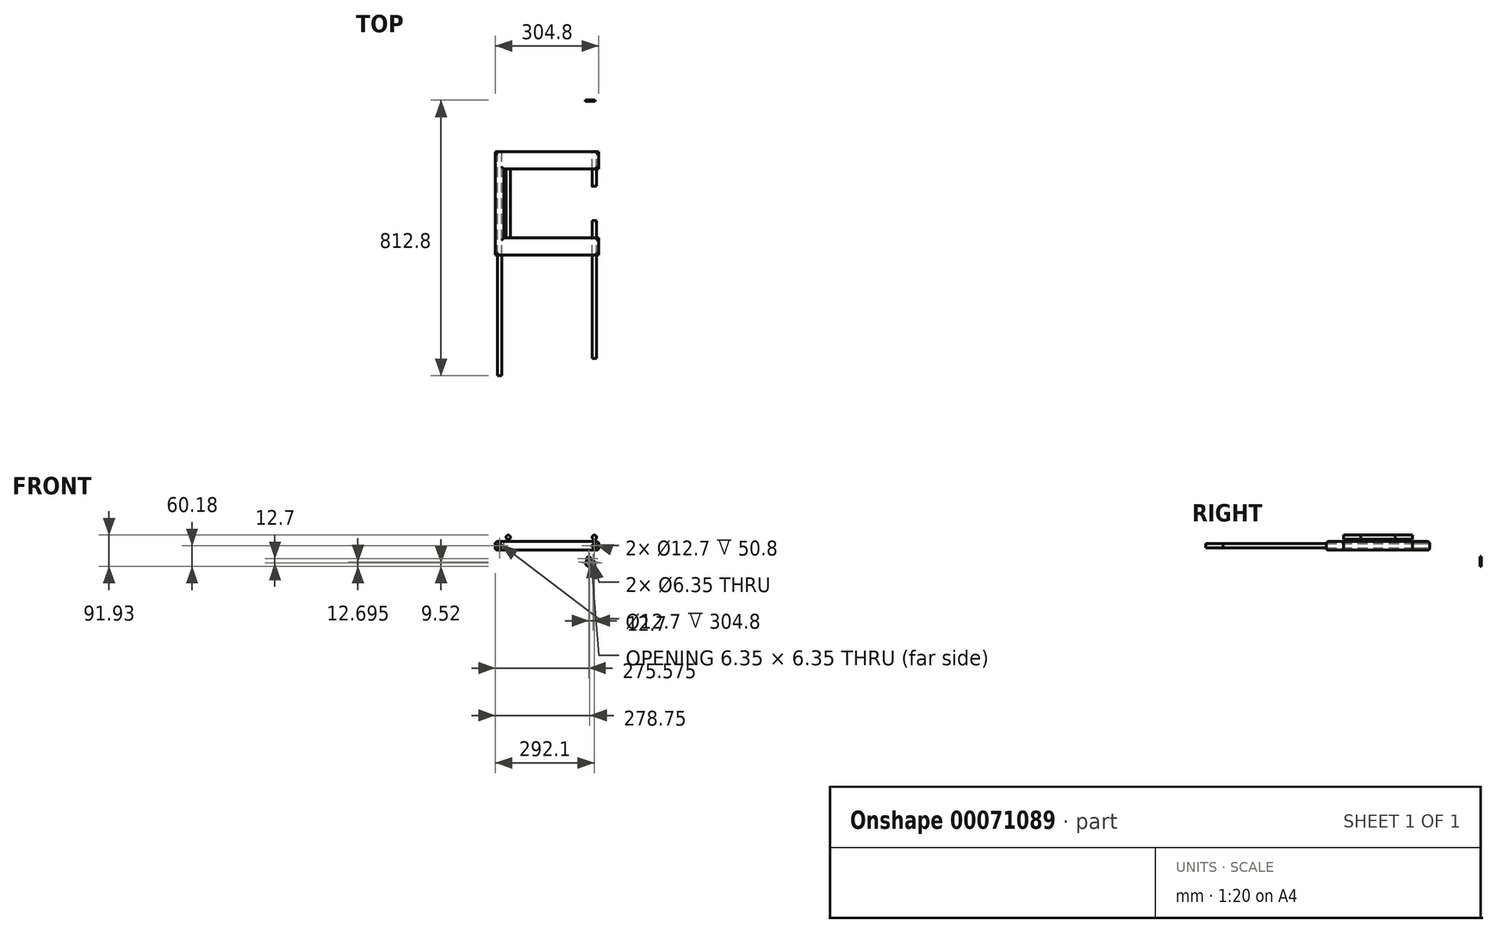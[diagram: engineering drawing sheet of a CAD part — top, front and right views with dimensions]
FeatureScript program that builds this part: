
annotation { "Feature Type Name" : "Feature", "Feature Type Description" : "" }
export const myFeature = defineFeature(function(context is Context, id is Id, definition is map)
    precondition{}
    {
        {
            var Q0;
            Q0=qCreatedBy(makeId("Front.planeOp"),FACE);
            var sketch = newSketch(context, id + "F0", { "sketchPlane" : qUnion([Q0])});
            skLineSegment(sketch, "E0.bottom", {"start": v(0, 0) * mm, "end": v(-304.8, 0) * mm});
            skLineSegment(sketch, "E0.top", {"start": v(0, 25.4) * mm, "end": v(-304.8, 25.4) * mm});
            skLineSegment(sketch, "E0.left", {"start": v(0, 0) * mm, "end": v(0, 25.4) * mm});
            skLineSegment(sketch, "E0.right", {"start": v(-304.8, 0) * mm, "end": v(-304.8, 25.4) * mm});
            skCircle(sketch, "E1", {"center": v(-12.7, 12.7) * mm, "radius": 6.35 * mm});
            skLineSegment(sketch, "E2", {"start": v(-152.4, 25.4) * mm, "end": v(-152.4, 0) * mm, "construction": true});
            skCircle(sketch, "E3.MirrorC", {"center": v(-292.1, 12.7) * mm, "radius": 6.35 * mm});
            skSolve(sketch);
        }
        {
            var Q0;
            Q0=makeQuery(id+"F0.imprint","IMPRINT",FACE,{"disambiguationData":[TD([[makeQuery(id+"F0.imprint","IMPRINT",EDGE,{"derivedFrom":sQuery(id+"F0.wireOp",EDGE,"E0.bottom")}),-1.0]])]});
            extrude(context, id + "F1", {"entities" : qUnion([Q0]), "depth" : 304.8 * mm});
        }
        {
            var Q0;
            Q0=makeQuery(id+"F1.opExtrude","SWEPT_FACE",FACE,{"disambiguationData":[OSD([sQuery(id+"F0.wireOp",EDGE,"E0.top")])]});
            var sketch = newSketch(context, id + "F2", { "sketchPlane" : qUnion([Q0])});
            skLineSegment(sketch, "E4.0", {"start": v(0, 0) * mm, "end": v(-304.8, 0) * mm});
            skLineSegment(sketch, "E4.1", {"start": v(-304.8, -304.8) * mm, "end": v(-304.8, 0) * mm});
            skLineSegment(sketch, "E4.2", {"start": v(0, -304.8) * mm, "end": v(0, 0) * mm});
            skLineSegment(sketch, "E4.3", {"start": v(0, -304.8) * mm, "end": v(-304.8, -304.8) * mm});
            skLineSegment(sketch, "E5.bottom", {"start": v(0, -50.8) * mm, "end": v(-279.4, -50.8) * mm});
            skLineSegment(sketch, "E5.top", {"start": v(0, -254) * mm, "end": v(-279.4, -254) * mm});
            skLineSegment(sketch, "E5.left", {"start": v(0, -50.8) * mm, "end": v(0, -254) * mm});
            skLineSegment(sketch, "E5.right", {"start": v(-279.4, -50.8) * mm, "end": v(-279.4, -254) * mm});
            skLineSegment(sketch, "E6.bottom", {"start": v(0, -101.6) * mm, "end": v(-254, -101.6) * mm});
            skLineSegment(sketch, "E6.top", {"start": v(0, -203.2) * mm, "end": v(-254, -203.2) * mm});
            skLineSegment(sketch, "E6.left", {"start": v(0, -101.6) * mm, "end": v(0, -203.2) * mm});
            skLineSegment(sketch, "E6.right", {"start": v(-254, -101.6) * mm, "end": v(-254, -203.2) * mm});
            skSolve(sketch);
        }
        {
            var Q0;
            {var subQ1=sQuery(id+"F2.wireOp",EDGE,"E5.bottom");Q0=makeQuery(id+"F2.imprint","IMPRINT",FACE,{"disambiguationData":[TD([[makeQuery(id+"F2.imprint","IMPRINT",EDGE,{"derivedFrom":subQ1}),1.0]])]});}
            extrude(context, id + "F3", {"entities" : qUnion([Q0]), "depth" : 25.4 * mm});
        }
        {
            var Q0;
            Q0=makeQuery(id+"F3.opExtrude","SWEPT_FACE",FACE,{"disambiguationData":[OSD([sQuery(id+"F2.wireOp",EDGE,"E5.bottom")])]});
            var sketch = newSketch(context, id + "F4", { "sketchPlane" : qUnion([Q0])});
            skCircle(sketch, "E7.0", {"center": v(12.7, 12.7) * mm, "radius": 6.35 * mm});
            skLineSegment(sketch, "E7.1.0", {"start": v(0, 0) * mm, "end": v(304.8, 0) * mm});
            skLineSegment(sketch, "E7.1.1", {"start": v(304.8, 0) * mm, "end": v(304.8, 25.4) * mm});
            skLineSegment(sketch, "E7.1.2", {"start": v(304.8, 25.4) * mm, "end": v(0, 25.4) * mm});
            skLineSegment(sketch, "E7.1.3", {"start": v(0, 25.4) * mm, "end": v(0, 0) * mm});
            skLineSegment(sketch, "E8", {"start": v(0, 25.4) * mm, "end": v(304.8, 25.4) * mm, "construction": true});
            skLineSegment(sketch, "E9", {"start": v(304.8, 25.4) * mm, "end": v(0, 25.4) * mm, "construction": true});
            skCircle(sketch, "E10.MirrorC", {"center": v(12.7, 38.1) * mm, "radius": 6.35 * mm});
            skLineSegment(sketch, "E11.0", {"start": v(0, 50.8) * mm, "end": v(279.4, 50.8) * mm});
            skLineSegment(sketch, "E12", {"start": v(139.7, 50.8) * mm, "end": v(139.7, 25.4) * mm, "construction": true});
            skCircle(sketch, "E13.MirrorC", {"center": v(266.7, 38.1) * mm, "radius": 6.35 * mm});
            skLineSegment(sketch, "E14", {"start": v(25.4, 25.4) * mm, "end": v(25.4, 50.8) * mm, "construction": true});
            skCircle(sketch, "E15.MirrorC", {"center": v(38.1, 38.1) * mm, "radius": 6.35 * mm});
            skSolve(sketch);
        }
        {
            var Q0;
            Q0=makeQuery(id+"F4.imprint","IMPRINT",FACE,{"disambiguationData":[TD([[makeQuery(id+"F4.imprint","IMPRINT",EDGE,{"derivedFrom":sQuery(id+"F4.wireOp",EDGE,"E10.MirrorC")}),-1.0]])]});
            var Q1;
            Q1=makeQuery(id+"F4.imprint","IMPRINT",FACE,{"disambiguationData":[TD([[makeQuery(id+"F4.imprint","IMPRINT",EDGE,{"derivedFrom":sQuery(id+"F4.wireOp",EDGE,"E15.MirrorC")}),1.0]])]});
            extrude(context, id + "F5", {"entities" : qUnion([Q0, Q1]), "operationType" : NewBodyOperationType.REMOVE, "endBound" : BoundingType.THROUGH_ALL, "oppositeDirection" : true, "depth" : 25.4 * mm});
        }
        {
            var Q0;
            {var subQ1=sQuery(id+"F2.wireOp",EDGE,"E5.bottom");Q0=makeQuery(id+"F2.imprint","IMPRINT",FACE,{"disambiguationData":[TD([[makeQuery(id+"F2.imprint","IMPRINT",EDGE,{"derivedFrom":subQ1}),1.0]])]});}
            var Q1;
            Q1=makeQuery(id+"F2.imprint","IMPRINT",FACE,{"disambiguationData":[TD([[makeQuery(id+"F2.imprint","IMPRINT",EDGE,{"derivedFrom":sQuery(id+"F2.wireOp",EDGE,"E6.bottom")}),1.0]])]});
            extrude(context, id + "F6", {"entities" : qUnion([Q0, Q1]), "operationType" : NewBodyOperationType.REMOVE, "endBound" : BoundingType.THROUGH_ALL, "oppositeDirection" : true, "depth" : 25.4 * mm});
        }
        {
            var Q0;
            Q0=makeQuery(id+"F1.opExtrude","CAP_FACE",FACE,{"disambiguationData":[OSD([sQuery(id+"F0.wireOp",EDGE,"E0.bottom"),sQuery(id+"F0.wireOp",EDGE,"E0.top"),sQuery(id+"F0.wireOp",EDGE,"E0.left"),sQuery(id+"F0.wireOp",EDGE,"E0.right"),sQuery(id+"F0.wireOp",EDGE,"E1"),sQuery(id+"F0.wireOp",EDGE,"E3.MirrorC")])],"isStart":false});
            var sketch = newSketch(context, id + "F7", { "sketchPlane" : qUnion([Q0])});
            skCircle(sketch, "E16.0", {"center": v(-12.7, 12.7) * mm, "radius": 6.35 * mm});
            skSolve(sketch);
        }
        {
            var Q0;
            Q0 = qSketchRegion(id + "F7", true);
            extrude(context, id + "F8", {"entities" : qUnion([Q0]), "depth" : 304.8 * mm});
        }
        {
            var Q0;
            Q0=makeQuery(id+"F1.opExtrude","CAP_FACE",FACE,{"disambiguationData":[OSD([sQuery(id+"F0.wireOp",EDGE,"E0.bottom"),sQuery(id+"F0.wireOp",EDGE,"E0.top"),sQuery(id+"F0.wireOp",EDGE,"E0.left"),sQuery(id+"F0.wireOp",EDGE,"E0.right"),sQuery(id+"F0.wireOp",EDGE,"E1"),sQuery(id+"F0.wireOp",EDGE,"E3.MirrorC")])],"isStart":false});
            var sketch = newSketch(context, id + "F9", { "sketchPlane" : qUnion([Q0])});
            skCircle(sketch, "E17.0", {"center": v(-292.1, 12.7) * mm, "radius": 6.35 * mm});
            skSolve(sketch);
        }
        {
            var Q0;
            Q0 = qSketchRegion(id + "F9", true);
            extrude(context, id + "F10", {"entities" : qUnion([Q0]), "depth" : 355.6 * mm});
        }
        {
            var Q0;
            Q0=makeQuery(id+"F1.opExtrude","SWEPT_FACE",FACE,{"disambiguationData":[OSD([sQuery(id+"F0.wireOp",EDGE,"E0.top")])]});
            var Q1;
            Q1=makeQuery(id+"F3.opExtrude","CAP_FACE",FACE,{"disambiguationData":[OSD([sQuery(id+"F2.wireOp",EDGE,"E5.bottom"),sQuery(id+"F2.wireOp",EDGE,"E5.top"),sQuery(id+"F2.wireOp",EDGE,"E5.left"),sQuery(id+"F2.wireOp",EDGE,"E5.right"),sQuery(id+"F2.wireOp",EDGE,"E6.bottom"),sQuery(id+"F2.wireOp",EDGE,"E6.top"),sQuery(id+"F2.wireOp",EDGE,"E6.right")])],"isStart":false});
            var Q2;
            Q2=makeQuery(id+"F1.opExtrude","SWEPT_FACE",FACE,{"disambiguationData":[OSD([sQuery(id+"F0.wireOp",EDGE,"E0.bottom")])]});
            var Q3;
            Q3=makeQuery(id+"F3.opExtrude","CAP_FACE",FACE,{"disambiguationData":[OSD([sQuery(id+"F2.wireOp",EDGE,"E5.bottom"),sQuery(id+"F2.wireOp",EDGE,"E5.top"),sQuery(id+"F2.wireOp",EDGE,"E5.left"),sQuery(id+"F2.wireOp",EDGE,"E5.right"),sQuery(id+"F2.wireOp",EDGE,"E6.bottom"),sQuery(id+"F2.wireOp",EDGE,"E6.top"),sQuery(id+"F2.wireOp",EDGE,"E6.right")])],"isStart":true});
            fillet(context, id + "F11", {"entities" : qUnion([Q0, Q1, Q2, Q3]), "radius" : 6.35 * mm, "tangentPropagation" : true, "allowEdgeOverflow" : false});
        }
        {
            var Q0;
            Q0=qCreatedBy(makeId("Front.planeOp"),FACE);
            cPlane(context, id + "F12", {"entities" : qUnion([Q0]), "cplaneType" : CPlaneType.OFFSET, "offset" : 152.4 * mm, "oppositeDirection" : true, "width" : 152.4 * mm, "height" : 152.4 * mm});
        }
        {
            var Q0;
            Q0=qCreatedBy(id+"F12.planeOp",FACE);
            var sketch = newSketch(context, id + "F13", { "sketchPlane" : qUnion([Q0])});
            skCircle(sketch, "E18", {"center": v(-29.23, -37.96) * mm, "radius": 6.35 * mm});
            skCircle(sketch, "E19", {"center": v(-16.53, -37.96) * mm, "radius": 6.35 * mm});
            skArc(sketch, "E20.0", {"start": v(-38.1, 31.75) * mm, "mid": v(-44.45, 38.1) * mm, "end": v(-38.1, 44.45) * mm});
            skArc(sketch, "E20.1", {"start": v(-38.1, 44.45) * mm, "mid": v(-31.75, 38.1) * mm, "end": v(-38.1, 31.75) * mm});
            skArc(sketch, "E21", {"start": v(-22.88, -37.96) * mm, "mid": v(-33.72, -42.45) * mm, "end": v(-29.23, -31.6) * mm});
            skArc(sketch, "E22", {"start": v(-10.18, -37.96) * mm, "mid": v(-42.7, -51.43) * mm, "end": v(-29.23, -18.9) * mm});
            skCircle(sketch, "E23", {"center": v(-29.23, -25.26) * mm, "radius": 6.35 * mm});
            skCircle(sketch, "E24", {"center": v(-29.23, -25.26) * mm, "radius": 3.18 * mm});
            skCircle(sketch, "E25", {"center": v(-16.53, -37.96) * mm, "radius": 3.18 * mm});
            skArc(sketch, "E26", {"start": v(-19.7, -37.96) * mm, "mid": v(-35.96, -44.7) * mm, "end": v(-29.23, -28.43) * mm});
            skArc(sketch, "E27", {"start": v(-13.35, -37.96) * mm, "mid": v(-40.45, -49.18) * mm, "end": v(-29.23, -22.08) * mm});
            skLineSegment(sketch, "E28", {"start": v(-22.88, -37.96) * mm, "end": v(-22.88, -37.96) * mm});
            skLineSegment(sketch, "E29", {"start": v(-29.23, -31.6) * mm, "end": v(-29.23, -31.6) * mm});
            skLineSegment(sketch, "E30", {"start": v(-22.88, -37.96) * mm, "end": v(-29.23, -31.6) * mm});
            skLineSegment(sketch, "E31", {"start": v(-21.15, -33.6) * mm, "end": v(-24.87, -29.88) * mm});
            skSolve(sketch);
        }
        {
            var Q0;
            {var subQ0=sQuery(id+"F13.wireOp",EDGE,"E22");Q0=makeQuery(id+"F13.imprint","IMPRINT",FACE,{"disambiguationData":[TD([[makeQuery(id+"F13.imprint","IMPRINT",EDGE,{"derivedFrom":subQ0}),-1.0]])]});}
            var Q1;
            {var subQ0=sQuery(id+"F13.wireOp",EDGE,"E21");Q1=makeQuery(id+"F13.imprint","IMPRINT",FACE,{"disambiguationData":[TD([[makeQuery(id+"F13.imprint","IMPRINT",EDGE,{"derivedFrom":subQ0}),1.0]])]});}
            var Q2;
            {var subQ0=sQuery(id+"F13.wireOp",EDGE,"E27");var subQ1=sQuery(id+"F13.wireOp",EDGE,"E23");var subQ2=makeQuery(id+"F13.imprint","INTERSECT",VERTEX,{"derivedFrom":[subQ1,subQ0]});Q2=makeQuery(id+"F13.imprint","IMPRINT",FACE,{"disambiguationData":[TD([[makeQuery(id+"F13.imprint","IMPRINT",EDGE,{"disambiguationData":[TD([[subQ2,-1.0]])],"derivedFrom":subQ1}),1.0]])]});}
            var Q3;
            {var subQ5=sQuery(id+"F13.wireOp",EDGE,"E23");var subQ8=makeQuery(id+"F13.imprint","INTERSECT",VERTEX,{"derivedFrom":[sQuery(id+"F13.wireOp",EDGE,"E22"),subQ5]});Q3=makeQuery(id+"F13.imprint","IMPRINT",FACE,{"disambiguationData":[TD([[makeQuery(id+"F13.imprint","IMPRINT",EDGE,{"disambiguationData":[TD([[subQ8,-1.0]])],"derivedFrom":subQ5}),1.0]])]});}
            var Q4;
            {var subQ5=sQuery(id+"F13.wireOp",EDGE,"E19");var subQ6=makeQuery(id+"F13.imprint","INTERSECT",VERTEX,{"derivedFrom":[subQ5,sQuery(id+"F13.wireOp",EDGE,"E21")]});Q4=makeQuery(id+"F13.imprint","IMPRINT",FACE,{"disambiguationData":[TD([[makeQuery(id+"F13.imprint","IMPRINT",EDGE,{"disambiguationData":[TD([[subQ6,1.0]])],"derivedFrom":subQ5}),1.0]])]});}
            var Q5;
            {var subQ0=sQuery(id+"F13.wireOp",EDGE,"E26");var subQ1=sQuery(id+"F13.wireOp",EDGE,"E19");var subQ2=makeQuery(id+"F13.imprint","INTERSECT",VERTEX,{"derivedFrom":[subQ1,subQ0]});Q5=makeQuery(id+"F13.imprint","IMPRINT",FACE,{"disambiguationData":[TD([[makeQuery(id+"F13.imprint","IMPRINT",EDGE,{"disambiguationData":[TD([[subQ2,-1.0]])],"derivedFrom":subQ1}),1.0]])]});}
            var Q6;
            {var subQ0=sQuery(id+"F13.wireOp",EDGE,"E28");Q6=makeQuery(id+"F13.imprint","IMPRINT",FACE,{"disambiguationData":[TD([[makeQuery(id+"F13.imprint","IMPRINT",EDGE,{"derivedFrom":subQ0}),1.0]])]});}
            var Q7;
            Q7=makeQuery(id+"F13.imprint","IMPRINT",FACE,{"disambiguationData":[TD([[makeQuery(id+"F13.imprint","IMPRINT",EDGE,{"derivedFrom":sQuery(id+"F13.wireOp",EDGE,"E21")}),-1.0]])]});
            var Q8;
            {var subQ1=sQuery(id+"F13.wireOp",EDGE,"E19");var subQ6=sQuery(id+"F13.wireOp",EDGE,"E26");var subQ7=makeQuery(id+"F13.imprint","INTERSECT",VERTEX,{"derivedFrom":[subQ1,subQ6]});Q8=makeQuery(id+"F13.imprint","IMPRINT",FACE,{"disambiguationData":[TD([[makeQuery(id+"F13.imprint","IMPRINT",EDGE,{"disambiguationData":[TD([[subQ7,-1.0]])],"derivedFrom":subQ6}),-1.0]])]});}
            var Q9;
            {var subQ6=sQuery(id+"F13.wireOp",EDGE,"E31");Q9=makeQuery(id+"F13.imprint","IMPRINT",FACE,{"disambiguationData":[TD([[makeQuery(id+"F13.imprint","IMPRINT",EDGE,{"derivedFrom":subQ6}),1.0]])]});}
            extrude(context, id + "F14", {"entities" : qUnion([Q0, Q1, Q2, Q3, Q4, Q5, Q6, Q7, Q8, Q9]), "depth" : 3.17 * mm});
        }
    });
